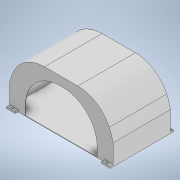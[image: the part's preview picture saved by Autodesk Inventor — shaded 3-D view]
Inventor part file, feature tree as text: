
AUTODESK INVENTOR PART (.ipt)
format: ipt  version: 2021 (Build 250183000, 183)  size: 222,208 bytes
history: native  units: mm
features: extrude x6, sketch x6, mirror x2, fillet x2, shell x1, plane x1
ambient origin geometry x8: Origin, YZ Plane, XZ Plane, XY Plane, X Axis, Y Axis, Z Axis, Center Point
bodies: Solid1 (feature_tree)
feature tree (18):
  extrude  "Extrusion1"  Depth=1000.0mm TaperAngle=0.0deg
  extrude  "Extrusion2"  Depth=1000.0mm
  mirror  "Mirror1"
  fillet  "Fillet1"  Radius=350.0mm
  sketch  "Sketch3"  dims[d9=0.0mm d10=600.0mm d11=150.0mm]
  shell  "Shell2"  Thickness=1000.0mm
  extrude  "Extrusion3"  Depth=600.0mm
  fillet  "Fillet2"  Radius=150.0mm
  extrude  "Extrusion4"  Depth=5.0mm
  extrude  "Extrusion5"  Depth=600.0mm
  extrude  "Extrusion6"  Depth=30.0mm
  mirror  "Mirror2"
  sketch  "Sketch1"  dims[d0=900.0mm d2=1000.0mm d3=0.0mm]
  sketch  "Sketch2"  dims[d5=900.0mm d6=550.0mm d7=350.0mm d8=1000.0mm]
  plane  "Work Plane1"
  sketch  "Sketch4"  dims[d12=600.0mm d13=5.0mm]
  sketch  "Sketch5"  dims[d14=10.0mm d15=0.0mm d16=600.0mm]
  sketch  "Sketch6"  dims[d17=10.0mm d18=0.0mm d19=30.0mm d20=150.0mm d23=50.0mm d24=0.0mm d25=20.0mm d29=30.0mm d30=0.0mm d31=1650.0mm d32=75.0mm]
